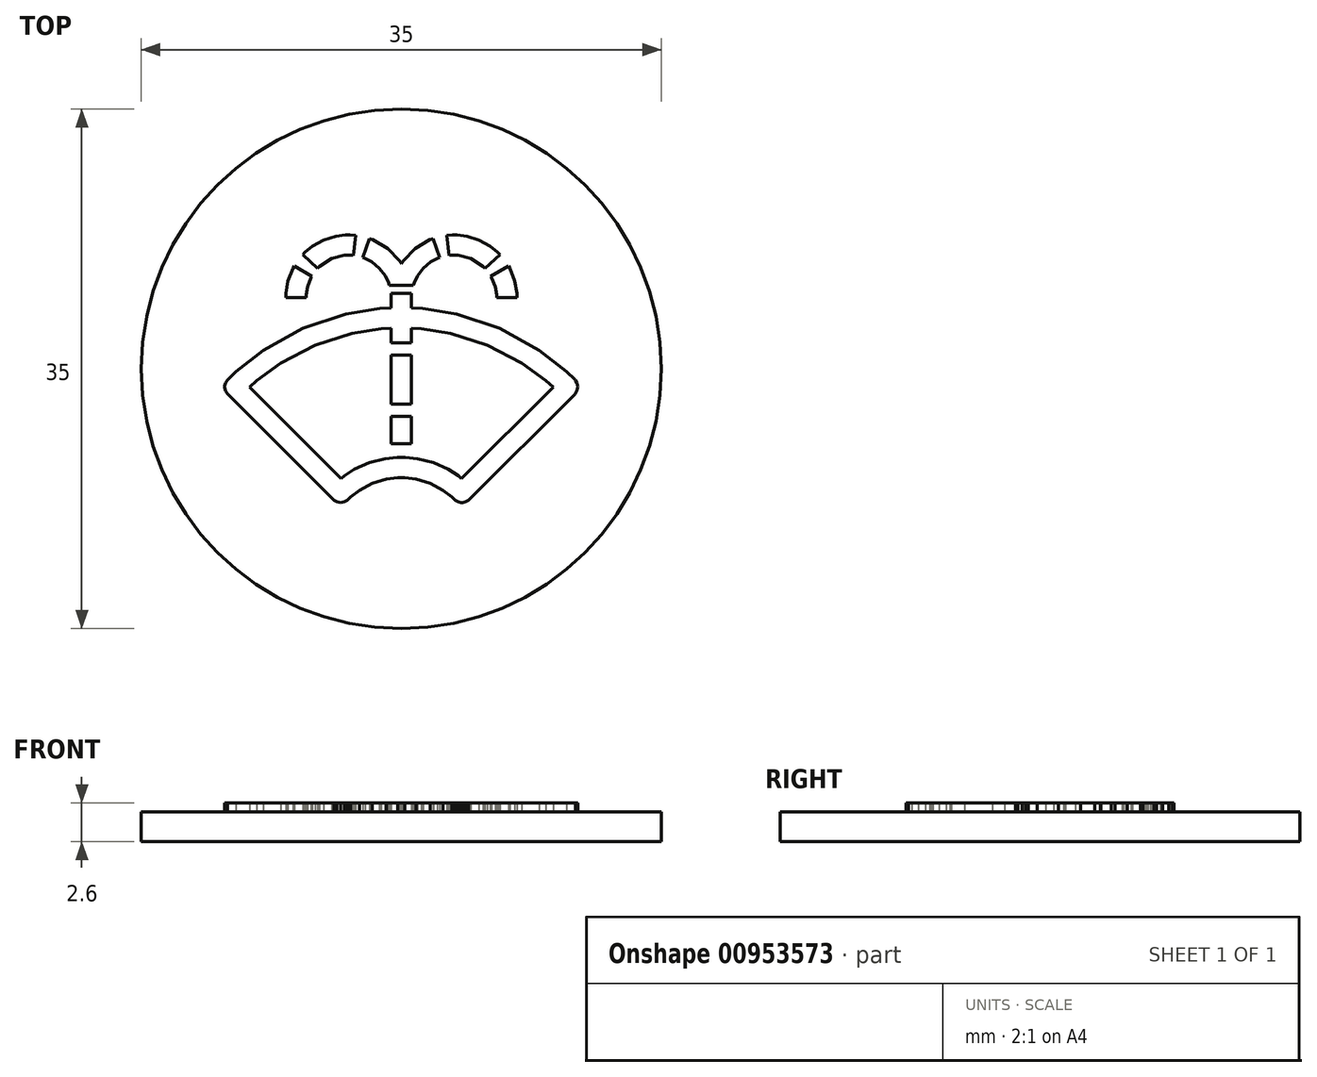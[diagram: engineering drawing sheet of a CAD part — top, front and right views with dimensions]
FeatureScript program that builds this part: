
annotation { "Feature Type Name" : "Feature", "Feature Type Description" : "" }
export const myFeature = defineFeature(function(context is Context, id is Id, definition is map)
    precondition{}
    {
        {
            assignVariable(context, id + "F0", {"name" : "size", "anyValue" : 35 * mm});
        }
        {
            assignVariable(context, id + "F1", {"name" : "scale", "anyValue" : getVariable(context, 'size') / (4 * mm)});
        }
        {
            var Q0;
            Q0=qCreatedBy(makeId("Top.planeOp"),FACE);
            var sketch = newSketch(context, id + "F2", { "sketchPlane" : qUnion([Q0])});
            skLineSegment(sketch, "E0", {"start": v(-0.69, 0.71) * mm, "end": v(-0.82, 0.8) * mm});
            skLineSegment(sketch, "E1", {"start": v(-0.82, 0.8) * mm, "end": v(-0.83, 0.77) * mm});
            skLineSegment(sketch, "E2", {"start": v(-0.83, 0.77) * mm, "end": v(-0.87, 0.67) * mm});
            skLineSegment(sketch, "E3", {"start": v(-0.87, 0.67) * mm, "end": v(-0.89, 0.58) * mm});
            skLineSegment(sketch, "E4", {"start": v(-0.89, 0.58) * mm, "end": v(-0.89, 0.55) * mm});
            skLineSegment(sketch, "E5", {"start": v(-0.89, 0.55) * mm, "end": v(-0.73, 0.55) * mm});
            skLineSegment(sketch, "E6", {"start": v(-0.73, 0.55) * mm, "end": v(-0.73, 0.57) * mm});
            skLineSegment(sketch, "E7", {"start": v(-0.73, 0.57) * mm, "end": v(-0.72, 0.63) * mm});
            skLineSegment(sketch, "E8", {"start": v(-0.72, 0.63) * mm, "end": v(-0.7, 0.7) * mm});
            skLineSegment(sketch, "E9", {"start": v(-0.7, 0.7) * mm, "end": v(-0.69, 0.71) * mm});
            skLineSegment(sketch, "E10", {"start": v(-0.4, 0.87) * mm, "end": v(-0.4, 0.87) * mm});
            skLineSegment(sketch, "E11", {"start": v(-0.4, 0.87) * mm, "end": v(-0.37, 0.87) * mm});
            skLineSegment(sketch, "E12", {"start": v(-0.37, 0.87) * mm, "end": v(-0.37, 0.87) * mm});
            skLineSegment(sketch, "E13", {"start": v(-0.37, 0.87) * mm, "end": v(-0.35, 1.03) * mm});
            skLineSegment(sketch, "E14", {"start": v(-0.35, 1.03) * mm, "end": v(-0.35, 1.03) * mm});
            skLineSegment(sketch, "E15", {"start": v(-0.35, 1.03) * mm, "end": v(-0.4, 1.03) * mm});
            skLineSegment(sketch, "E16", {"start": v(-0.4, 1.03) * mm, "end": v(-0.4, 1.03) * mm});
            skLineSegment(sketch, "E17", {"start": v(-0.4, 1.03) * mm, "end": v(-0.43, 1.03) * mm});
            skLineSegment(sketch, "E18", {"start": v(-0.43, 1.03) * mm, "end": v(-0.5, 1.02) * mm});
            skLineSegment(sketch, "E19", {"start": v(-0.5, 1.02) * mm, "end": v(-0.6, 1) * mm});
            skLineSegment(sketch, "E20", {"start": v(-0.6, 1) * mm, "end": v(-0.68, 0.94) * mm});
            skLineSegment(sketch, "E21", {"start": v(-0.68, 0.94) * mm, "end": v(-0.74, 0.9) * mm});
            skLineSegment(sketch, "E22", {"start": v(-0.74, 0.9) * mm, "end": v(-0.76, 0.88) * mm});
            skLineSegment(sketch, "E23", {"start": v(-0.76, 0.88) * mm, "end": v(-0.64, 0.77) * mm});
            skLineSegment(sketch, "E24", {"start": v(-0.64, 0.77) * mm, "end": v(-0.63, 0.79) * mm});
            skLineSegment(sketch, "E25", {"start": v(-0.63, 0.79) * mm, "end": v(-0.54, 0.85) * mm});
            skLineSegment(sketch, "E26", {"start": v(-0.54, 0.85) * mm, "end": v(-0.44, 0.87) * mm});
            skLineSegment(sketch, "E27", {"start": v(-0.44, 0.87) * mm, "end": v(-0.4, 0.87) * mm});
            skLineSegment(sketch, "E28", {"start": v(-0.1, 0.64) * mm, "end": v(0.1, 0.64) * mm});
            skLineSegment(sketch, "E29", {"start": v(0.1, 0.64) * mm, "end": v(0.1, 0.66) * mm});
            skLineSegment(sketch, "E30", {"start": v(0.1, 0.66) * mm, "end": v(0.12, 0.71) * mm});
            skLineSegment(sketch, "E31", {"start": v(0.12, 0.71) * mm, "end": v(0.17, 0.77) * mm});
            skLineSegment(sketch, "E32", {"start": v(0.17, 0.77) * mm, "end": v(0.23, 0.82) * mm});
            skLineSegment(sketch, "E33", {"start": v(0.23, 0.82) * mm, "end": v(0.28, 0.85) * mm});
            skLineSegment(sketch, "E34", {"start": v(0.28, 0.85) * mm, "end": v(0.3, 0.86) * mm});
            skLineSegment(sketch, "E35", {"start": v(0.3, 0.86) * mm, "end": v(0.24, 1) * mm});
            skLineSegment(sketch, "E36", {"start": v(0.24, 1) * mm, "end": v(0.22, 1) * mm});
            skLineSegment(sketch, "E37", {"start": v(0.22, 1) * mm, "end": v(0.1, 0.93) * mm});
            skLineSegment(sketch, "E38", {"start": v(0.1, 0.93) * mm, "end": v(0.01, 0.83) * mm});
            skLineSegment(sketch, "E39", {"start": v(0.01, 0.83) * mm, "end": v(0, 0.81) * mm});
            skLineSegment(sketch, "E40", {"start": v(0, 0.81) * mm, "end": v(-0.01, 0.83) * mm});
            skLineSegment(sketch, "E41", {"start": v(-0.01, 0.83) * mm, "end": v(-0.1, 0.93) * mm});
            skLineSegment(sketch, "E42", {"start": v(-0.1, 0.93) * mm, "end": v(-0.22, 1) * mm});
            skLineSegment(sketch, "E43", {"start": v(-0.22, 1) * mm, "end": v(-0.24, 1) * mm});
            skLineSegment(sketch, "E44", {"start": v(-0.24, 1) * mm, "end": v(-0.3, 0.86) * mm});
            skLineSegment(sketch, "E45", {"start": v(-0.3, 0.86) * mm, "end": v(-0.28, 0.85) * mm});
            skLineSegment(sketch, "E46", {"start": v(-0.28, 0.85) * mm, "end": v(-0.23, 0.82) * mm});
            skLineSegment(sketch, "E47", {"start": v(-0.23, 0.82) * mm, "end": v(-0.17, 0.77) * mm});
            skLineSegment(sketch, "E48", {"start": v(-0.17, 0.77) * mm, "end": v(-0.12, 0.71) * mm});
            skLineSegment(sketch, "E49", {"start": v(-0.12, 0.71) * mm, "end": v(-0.1, 0.66) * mm});
            skLineSegment(sketch, "E50", {"start": v(-0.1, 0.66) * mm, "end": v(-0.1, 0.64) * mm});
            skLineSegment(sketch, "E51", {"start": v(0.73, 0.55) * mm, "end": v(0.89, 0.55) * mm});
            skLineSegment(sketch, "E52", {"start": v(0.89, 0.55) * mm, "end": v(0.89, 0.58) * mm});
            skLineSegment(sketch, "E53", {"start": v(0.89, 0.58) * mm, "end": v(0.87, 0.67) * mm});
            skLineSegment(sketch, "E54", {"start": v(0.87, 0.67) * mm, "end": v(0.83, 0.77) * mm});
            skLineSegment(sketch, "E55", {"start": v(0.83, 0.77) * mm, "end": v(0.82, 0.8) * mm});
            skLineSegment(sketch, "E56", {"start": v(0.82, 0.8) * mm, "end": v(0.69, 0.71) * mm});
            skLineSegment(sketch, "E57", {"start": v(0.69, 0.71) * mm, "end": v(0.7, 0.7) * mm});
            skLineSegment(sketch, "E58", {"start": v(0.7, 0.7) * mm, "end": v(0.72, 0.63) * mm});
            skLineSegment(sketch, "E59", {"start": v(0.72, 0.63) * mm, "end": v(0.73, 0.57) * mm});
            skLineSegment(sketch, "E60", {"start": v(0.73, 0.57) * mm, "end": v(0.73, 0.55) * mm});
            skLineSegment(sketch, "E61", {"start": v(-0.08, 0.1) * mm, "end": v(0.08, 0.1) * mm});
            skLineSegment(sketch, "E62", {"start": v(0.08, 0.1) * mm, "end": v(0.08, -0.27) * mm});
            skLineSegment(sketch, "E63", {"start": v(0.08, -0.27) * mm, "end": v(-0.08, -0.27) * mm});
            skLineSegment(sketch, "E64", {"start": v(-0.08, -0.27) * mm, "end": v(-0.08, 0.1) * mm});
            skLineSegment(sketch, "E65", {"start": v(0.4, 0.87) * mm, "end": v(0.44, 0.87) * mm});
            skLineSegment(sketch, "E66", {"start": v(0.44, 0.87) * mm, "end": v(0.54, 0.85) * mm});
            skLineSegment(sketch, "E67", {"start": v(0.54, 0.85) * mm, "end": v(0.63, 0.79) * mm});
            skLineSegment(sketch, "E68", {"start": v(0.63, 0.79) * mm, "end": v(0.64, 0.77) * mm});
            skLineSegment(sketch, "E69", {"start": v(0.64, 0.77) * mm, "end": v(0.76, 0.88) * mm});
            skLineSegment(sketch, "E70", {"start": v(0.76, 0.88) * mm, "end": v(0.74, 0.9) * mm});
            skLineSegment(sketch, "E71", {"start": v(0.74, 0.9) * mm, "end": v(0.68, 0.94) * mm});
            skLineSegment(sketch, "E72", {"start": v(0.68, 0.94) * mm, "end": v(0.6, 1) * mm});
            skLineSegment(sketch, "E73", {"start": v(0.6, 1) * mm, "end": v(0.5, 1.02) * mm});
            skLineSegment(sketch, "E74", {"start": v(0.5, 1.02) * mm, "end": v(0.43, 1.03) * mm});
            skLineSegment(sketch, "E75", {"start": v(0.43, 1.03) * mm, "end": v(0.4, 1.03) * mm});
            skLineSegment(sketch, "E76", {"start": v(0.4, 1.03) * mm, "end": v(0.4, 1.03) * mm});
            skLineSegment(sketch, "E77", {"start": v(0.4, 1.03) * mm, "end": v(0.36, 1.03) * mm});
            skLineSegment(sketch, "E78", {"start": v(0.36, 1.03) * mm, "end": v(0.35, 1.03) * mm});
            skLineSegment(sketch, "E79", {"start": v(0.35, 1.03) * mm, "end": v(0.37, 0.87) * mm});
            skLineSegment(sketch, "E80", {"start": v(0.37, 0.87) * mm, "end": v(0.37, 0.87) * mm});
            skLineSegment(sketch, "E81", {"start": v(0.37, 0.87) * mm, "end": v(0.4, 0.87) * mm});
            skLineSegment(sketch, "E82", {"start": v(0.4, 0.87) * mm, "end": v(0.4, 0.87) * mm});
            skLineSegment(sketch, "E83", {"start": v(-0.08, -0.37) * mm, "end": v(0.08, -0.37) * mm});
            skLineSegment(sketch, "E84", {"start": v(0.08, -0.37) * mm, "end": v(0.08, -0.58) * mm});
            skLineSegment(sketch, "E85", {"start": v(0.08, -0.58) * mm, "end": v(-0.08, -0.58) * mm});
            skLineSegment(sketch, "E86", {"start": v(-0.08, -0.58) * mm, "end": v(-0.08, -0.37) * mm});
            skLineSegment(sketch, "E87", {"start": v(0.08, 0.47) * mm, "end": v(0.08, 0.58) * mm});
            skLineSegment(sketch, "E88", {"start": v(0.08, 0.58) * mm, "end": v(-0.08, 0.58) * mm});
            skLineSegment(sketch, "E89", {"start": v(-0.08, 0.58) * mm, "end": v(-0.08, 0.47) * mm});
            skLineSegment(sketch, "E90", {"start": v(-0.08, 0.47) * mm, "end": v(-0.17, 0.46) * mm});
            skLineSegment(sketch, "E91", {"start": v(-0.17, 0.46) * mm, "end": v(-0.43, 0.42) * mm});
            skLineSegment(sketch, "E92", {"start": v(-0.43, 0.42) * mm, "end": v(-0.76, 0.31) * mm});
            skLineSegment(sketch, "E93", {"start": v(-0.76, 0.31) * mm, "end": v(-1.06, 0.14) * mm});
            skLineSegment(sketch, "E94", {"start": v(-1.06, 0.14) * mm, "end": v(-1.27, -0.02) * mm});
            skLineSegment(sketch, "E95", {"start": v(-1.27, -0.02) * mm, "end": v(-1.33, -0.08) * mm});
            skLineSegment(sketch, "E96", {"start": v(-1.33, -0.08) * mm, "end": v(-1.34, -0.09) * mm});
            skLineSegment(sketch, "E97", {"start": v(-1.34, -0.09) * mm, "end": v(-1.35, -0.1) * mm});
            skLineSegment(sketch, "E98", {"start": v(-1.35, -0.1) * mm, "end": v(-1.36, -0.13) * mm});
            skLineSegment(sketch, "E99", {"start": v(-1.36, -0.13) * mm, "end": v(-1.36, -0.14) * mm});
            skLineSegment(sketch, "E100", {"start": v(-1.36, -0.14) * mm, "end": v(-1.36, -0.15) * mm});
            skLineSegment(sketch, "E101", {"start": v(-1.36, -0.15) * mm, "end": v(-1.35, -0.17) * mm});
            skLineSegment(sketch, "E102", {"start": v(-1.35, -0.17) * mm, "end": v(-1.34, -0.2) * mm});
            skLineSegment(sketch, "E103", {"start": v(-1.34, -0.2) * mm, "end": v(-1.33, -0.2) * mm});
            skLineSegment(sketch, "E104", {"start": v(-1.33, -0.2) * mm, "end": v(-0.52, -1) * mm});
            skLineSegment(sketch, "E105", {"start": v(-0.52, -1) * mm, "end": v(-0.52, -1.01) * mm});
            skLineSegment(sketch, "E106", {"start": v(-0.52, -1.01) * mm, "end": v(-0.5, -1.02) * mm});
            skLineSegment(sketch, "E107", {"start": v(-0.5, -1.02) * mm, "end": v(-0.47, -1.03) * mm});
            skLineSegment(sketch, "E108", {"start": v(-0.47, -1.03) * mm, "end": v(-0.44, -1.02) * mm});
            skLineSegment(sketch, "E109", {"start": v(-0.44, -1.02) * mm, "end": v(-0.42, -1.01) * mm});
            skLineSegment(sketch, "E110", {"start": v(-0.42, -1.01) * mm, "end": v(-0.41, -1) * mm});
            skLineSegment(sketch, "E111", {"start": v(-0.41, -1) * mm, "end": v(-0.4, -0.99) * mm});
            skLineSegment(sketch, "E112", {"start": v(-0.4, -0.99) * mm, "end": v(-0.32, -0.93) * mm});
            skLineSegment(sketch, "E113", {"start": v(-0.32, -0.93) * mm, "end": v(-0.22, -0.88) * mm});
            skLineSegment(sketch, "E114", {"start": v(-0.22, -0.88) * mm, "end": v(-0.11, -0.85) * mm});
            skLineSegment(sketch, "E115", {"start": v(-0.11, -0.85) * mm, "end": v(-0.03, -0.84) * mm});
            skLineSegment(sketch, "E116", {"start": v(-0.03, -0.84) * mm, "end": v(0, -0.84) * mm});
            skLineSegment(sketch, "E117", {"start": v(0, -0.84) * mm, "end": v(0.03, -0.84) * mm});
            skLineSegment(sketch, "E118", {"start": v(0.03, -0.84) * mm, "end": v(0.11, -0.85) * mm});
            skLineSegment(sketch, "E119", {"start": v(0.11, -0.85) * mm, "end": v(0.22, -0.88) * mm});
            skLineSegment(sketch, "E120", {"start": v(0.22, -0.88) * mm, "end": v(0.32, -0.93) * mm});
            skLineSegment(sketch, "E121", {"start": v(0.32, -0.93) * mm, "end": v(0.4, -0.99) * mm});
            skLineSegment(sketch, "E122", {"start": v(0.4, -0.99) * mm, "end": v(0.41, -1) * mm});
            skLineSegment(sketch, "E123", {"start": v(0.41, -1) * mm, "end": v(0.41, -1.01) * mm});
            skLineSegment(sketch, "E124", {"start": v(0.41, -1.01) * mm, "end": v(0.44, -1.02) * mm});
            skLineSegment(sketch, "E125", {"start": v(0.44, -1.02) * mm, "end": v(0.46, -1.03) * mm});
            skLineSegment(sketch, "E126", {"start": v(0.46, -1.03) * mm, "end": v(0.47, -1.03) * mm});
            skLineSegment(sketch, "E127", {"start": v(0.47, -1.03) * mm, "end": v(0.47, -1.03) * mm});
            skLineSegment(sketch, "E128", {"start": v(0.47, -1.03) * mm, "end": v(0.5, -1.02) * mm});
            skLineSegment(sketch, "E129", {"start": v(0.5, -1.02) * mm, "end": v(0.52, -1.01) * mm});
            skLineSegment(sketch, "E130", {"start": v(0.52, -1.01) * mm, "end": v(0.52, -1) * mm});
            skLineSegment(sketch, "E131", {"start": v(0.52, -1) * mm, "end": v(1.33, -0.2) * mm});
            skLineSegment(sketch, "E132", {"start": v(1.33, -0.2) * mm, "end": v(1.34, -0.19) * mm});
            skLineSegment(sketch, "E133", {"start": v(1.34, -0.19) * mm, "end": v(1.35, -0.17) * mm});
            skLineSegment(sketch, "E134", {"start": v(1.35, -0.17) * mm, "end": v(1.36, -0.14) * mm});
            skLineSegment(sketch, "E135", {"start": v(1.36, -0.14) * mm, "end": v(1.35, -0.1) * mm});
            skLineSegment(sketch, "E136", {"start": v(1.35, -0.1) * mm, "end": v(1.34, -0.09) * mm});
            skLineSegment(sketch, "E137", {"start": v(1.34, -0.09) * mm, "end": v(1.33, -0.08) * mm});
            skLineSegment(sketch, "E138", {"start": v(1.33, -0.08) * mm, "end": v(1.27, -0.02) * mm});
            skLineSegment(sketch, "E139", {"start": v(1.27, -0.02) * mm, "end": v(1.06, 0.14) * mm});
            skLineSegment(sketch, "E140", {"start": v(1.06, 0.14) * mm, "end": v(0.76, 0.31) * mm});
            skLineSegment(sketch, "E141", {"start": v(0.76, 0.31) * mm, "end": v(0.43, 0.42) * mm});
            skLineSegment(sketch, "E142", {"start": v(0.43, 0.42) * mm, "end": v(0.17, 0.46) * mm});
            skLineSegment(sketch, "E143", {"start": v(0.17, 0.46) * mm, "end": v(0.08, 0.47) * mm});
            skLineSegment(sketch, "E144", {"start": v(0.46, -0.84) * mm, "end": v(0.44, -0.83) * mm});
            skLineSegment(sketch, "E145", {"start": v(0.44, -0.83) * mm, "end": v(0.36, -0.77) * mm});
            skLineSegment(sketch, "E146", {"start": v(0.36, -0.77) * mm, "end": v(0.25, -0.72) * mm});
            skLineSegment(sketch, "E147", {"start": v(0.25, -0.72) * mm, "end": v(0.13, -0.7) * mm});
            skLineSegment(sketch, "E148", {"start": v(0.13, -0.7) * mm, "end": v(0.03, -0.68) * mm});
            skLineSegment(sketch, "E149", {"start": v(0.03, -0.68) * mm, "end": v(0, -0.68) * mm});
            skLineSegment(sketch, "E150", {"start": v(0, -0.68) * mm, "end": v(-0.03, -0.68) * mm});
            skLineSegment(sketch, "E151", {"start": v(-0.03, -0.68) * mm, "end": v(-0.13, -0.7) * mm});
            skLineSegment(sketch, "E152", {"start": v(-0.13, -0.7) * mm, "end": v(-0.25, -0.72) * mm});
            skLineSegment(sketch, "E153", {"start": v(-0.25, -0.72) * mm, "end": v(-0.36, -0.77) * mm});
            skLineSegment(sketch, "E154", {"start": v(-0.36, -0.77) * mm, "end": v(-0.44, -0.83) * mm});
            skLineSegment(sketch, "E155", {"start": v(-0.44, -0.83) * mm, "end": v(-0.46, -0.84) * mm});
            skLineSegment(sketch, "E156", {"start": v(-0.46, -0.84) * mm, "end": v(-1.17, -0.14) * mm});
            skLineSegment(sketch, "E157", {"start": v(-1.17, -0.14) * mm, "end": v(-1.11, -0.09) * mm});
            skLineSegment(sketch, "E158", {"start": v(-1.11, -0.09) * mm, "end": v(-0.93, 0.04) * mm});
            skLineSegment(sketch, "E159", {"start": v(-0.93, 0.04) * mm, "end": v(-0.66, 0.18) * mm});
            skLineSegment(sketch, "E160", {"start": v(-0.66, 0.18) * mm, "end": v(-0.38, 0.27) * mm});
            skLineSegment(sketch, "E161", {"start": v(-0.38, 0.27) * mm, "end": v(-0.15, 0.3) * mm});
            skLineSegment(sketch, "E162", {"start": v(-0.15, 0.3) * mm, "end": v(-0.08, 0.31) * mm});
            skLineSegment(sketch, "E163", {"start": v(-0.08, 0.31) * mm, "end": v(-0.08, 0.2) * mm});
            skLineSegment(sketch, "E164", {"start": v(-0.08, 0.2) * mm, "end": v(0.08, 0.2) * mm});
            skLineSegment(sketch, "E165", {"start": v(0.08, 0.2) * mm, "end": v(0.08, 0.31) * mm});
            skLineSegment(sketch, "E166", {"start": v(0.08, 0.31) * mm, "end": v(0.15, 0.3) * mm});
            skLineSegment(sketch, "E167", {"start": v(0.15, 0.3) * mm, "end": v(0.38, 0.27) * mm});
            skLineSegment(sketch, "E168", {"start": v(0.38, 0.27) * mm, "end": v(0.66, 0.18) * mm});
            skLineSegment(sketch, "E169", {"start": v(0.66, 0.18) * mm, "end": v(0.93, 0.04) * mm});
            skLineSegment(sketch, "E170", {"start": v(0.93, 0.04) * mm, "end": v(1.11, -0.09) * mm});
            skLineSegment(sketch, "E171", {"start": v(1.11, -0.09) * mm, "end": v(1.17, -0.14) * mm});
            skLineSegment(sketch, "E172", {"start": v(1.17, -0.14) * mm, "end": v(0.46, -0.84) * mm});
            skCircle(sketch, "E173", {"center": v(0, 0) * mm, "radius": 2 * mm});
            skSolve(sketch);
        }
        {
            var Q0;
            Q0=makeQuery(id+"F2.imprint","IMPRINT",FACE,{"disambiguationData":[TD([[makeQuery(id+"F2.imprint","IMPRINT",EDGE,{"derivedFrom":sQuery(id+"F2.wireOp",EDGE,"E0")}),-1.0]])]});
            var Q1;
            Q1=makeQuery(id+"F2.imprint","IMPRINT",FACE,{"disambiguationData":[TD([[makeQuery(id+"F2.imprint","IMPRINT",EDGE,{"derivedFrom":sQuery(id+"F2.wireOp",EDGE,"E61")}),1.0]])]});
            var Q2;
            Q2=makeQuery(id+"F2.imprint","IMPRINT",FACE,{"disambiguationData":[TD([[makeQuery(id+"F2.imprint","IMPRINT",EDGE,{"derivedFrom":sQuery(id+"F2.wireOp",EDGE,"E87")}),1.0]])]});
            var Q3;
            Q3=makeQuery(id+"F2.imprint","IMPRINT",FACE,{"disambiguationData":[TD([[makeQuery(id+"F2.imprint","IMPRINT",EDGE,{"derivedFrom":sQuery(id+"F2.wireOp",EDGE,"E0")}),1.0]])]});
            var Q4;
            Q4=makeQuery(id+"F2.imprint","IMPRINT",FACE,{"disambiguationData":[TD([[makeQuery(id+"F2.imprint","IMPRINT",EDGE,{"derivedFrom":sQuery(id+"F2.wireOp",EDGE,"E28")}),1.0]])]});
            var Q5;
            Q5=makeQuery(id+"F2.imprint","IMPRINT",FACE,{"disambiguationData":[TD([[makeQuery(id+"F2.imprint","IMPRINT",EDGE,{"derivedFrom":sQuery(id+"F2.wireOp",EDGE,"E10")}),1.0]])]});
            var Q6;
            Q6=makeQuery(id+"F2.imprint","IMPRINT",FACE,{"disambiguationData":[TD([[makeQuery(id+"F2.imprint","IMPRINT",EDGE,{"derivedFrom":sQuery(id+"F2.wireOp",EDGE,"E65")}),1.0]])]});
            var Q7;
            Q7=makeQuery(id+"F2.imprint","IMPRINT",FACE,{"disambiguationData":[TD([[makeQuery(id+"F2.imprint","IMPRINT",EDGE,{"derivedFrom":sQuery(id+"F2.wireOp",EDGE,"E51")}),1.0]])]});
            var Q8;
            Q8=makeQuery(id+"F2.imprint","IMPRINT",FACE,{"disambiguationData":[TD([[makeQuery(id+"F2.imprint","IMPRINT",EDGE,{"derivedFrom":sQuery(id+"F2.wireOp",EDGE,"E61")}),-1.0]])]});
            var Q9;
            Q9=makeQuery(id+"F2.imprint","IMPRINT",FACE,{"disambiguationData":[TD([[makeQuery(id+"F2.imprint","IMPRINT",EDGE,{"derivedFrom":sQuery(id+"F2.wireOp",EDGE,"E83")}),-1.0]])]});
            extrude(context, id + "F3", {"entities" : qUnion([Q0, Q1, Q2, Q3, Q4, Q5, Q6, Q7, Q8, Q9]), "oppositeDirection" : true, "depth" : 2 * mm / getVariable(context, 'scale'), "offsetDistance" : 25 * mm});
        }
        {
            var Q0;
            Q0=makeQuery(id+"F2.imprint","IMPRINT",FACE,{"disambiguationData":[TD([[makeQuery(id+"F2.imprint","IMPRINT",EDGE,{"derivedFrom":sQuery(id+"F2.wireOp",EDGE,"E87")}),1.0]])]});
            var Q1;
            Q1=makeQuery(id+"F2.imprint","IMPRINT",FACE,{"disambiguationData":[TD([[makeQuery(id+"F2.imprint","IMPRINT",EDGE,{"derivedFrom":sQuery(id+"F2.wireOp",EDGE,"E61")}),-1.0]])]});
            var Q2;
            Q2=makeQuery(id+"F2.imprint","IMPRINT",FACE,{"disambiguationData":[TD([[makeQuery(id+"F2.imprint","IMPRINT",EDGE,{"derivedFrom":sQuery(id+"F2.wireOp",EDGE,"E83")}),-1.0]])]});
            var Q3;
            Q3=makeQuery(id+"F2.imprint","IMPRINT",FACE,{"disambiguationData":[TD([[makeQuery(id+"F2.imprint","IMPRINT",EDGE,{"derivedFrom":sQuery(id+"F2.wireOp",EDGE,"E28")}),1.0]])]});
            var Q4;
            Q4=makeQuery(id+"F2.imprint","IMPRINT",FACE,{"disambiguationData":[TD([[makeQuery(id+"F2.imprint","IMPRINT",EDGE,{"derivedFrom":sQuery(id+"F2.wireOp",EDGE,"E10")}),1.0]])]});
            var Q5;
            Q5=makeQuery(id+"F2.imprint","IMPRINT",FACE,{"disambiguationData":[TD([[makeQuery(id+"F2.imprint","IMPRINT",EDGE,{"derivedFrom":sQuery(id+"F2.wireOp",EDGE,"E0")}),1.0]])]});
            var Q6;
            Q6=makeQuery(id+"F2.imprint","IMPRINT",FACE,{"disambiguationData":[TD([[makeQuery(id+"F2.imprint","IMPRINT",EDGE,{"derivedFrom":sQuery(id+"F2.wireOp",EDGE,"E65")}),1.0]])]});
            var Q7;
            Q7=makeQuery(id+"F2.imprint","IMPRINT",FACE,{"disambiguationData":[TD([[makeQuery(id+"F2.imprint","IMPRINT",EDGE,{"derivedFrom":sQuery(id+"F2.wireOp",EDGE,"E51")}),1.0]])]});
            extrude(context, id + "F4", {"entities" : qUnion([Q0, Q1, Q2, Q3, Q4, Q5, Q6, Q7]), "operationType" : NewBodyOperationType.ADD, "depth" : 0.6 * mm / getVariable(context, 'scale'), "offsetDistance" : 25 * mm});
        }
        {
            var Q0;
            Q0=makeQuery(id+"F3.opExtrude","SWEPT_BODY",BODY,{"disambiguationData":[OSD([sQuery(id+"F2.wireOp",EDGE,"E173")])]});
            var Q1;
            Q1=sQuery(id+"F2.wireOp",VERTEX,"E173.center");
            transform(context, id + "F5", {"entities" : qUnion([Q0]), "transformType" : TransformType.SCALE_UNIFORMLY, "scale" : getVariable(context, 'scale'), "scalePoint" : qUnion([Q1]), "makeCopy" : false});
        }
    });
